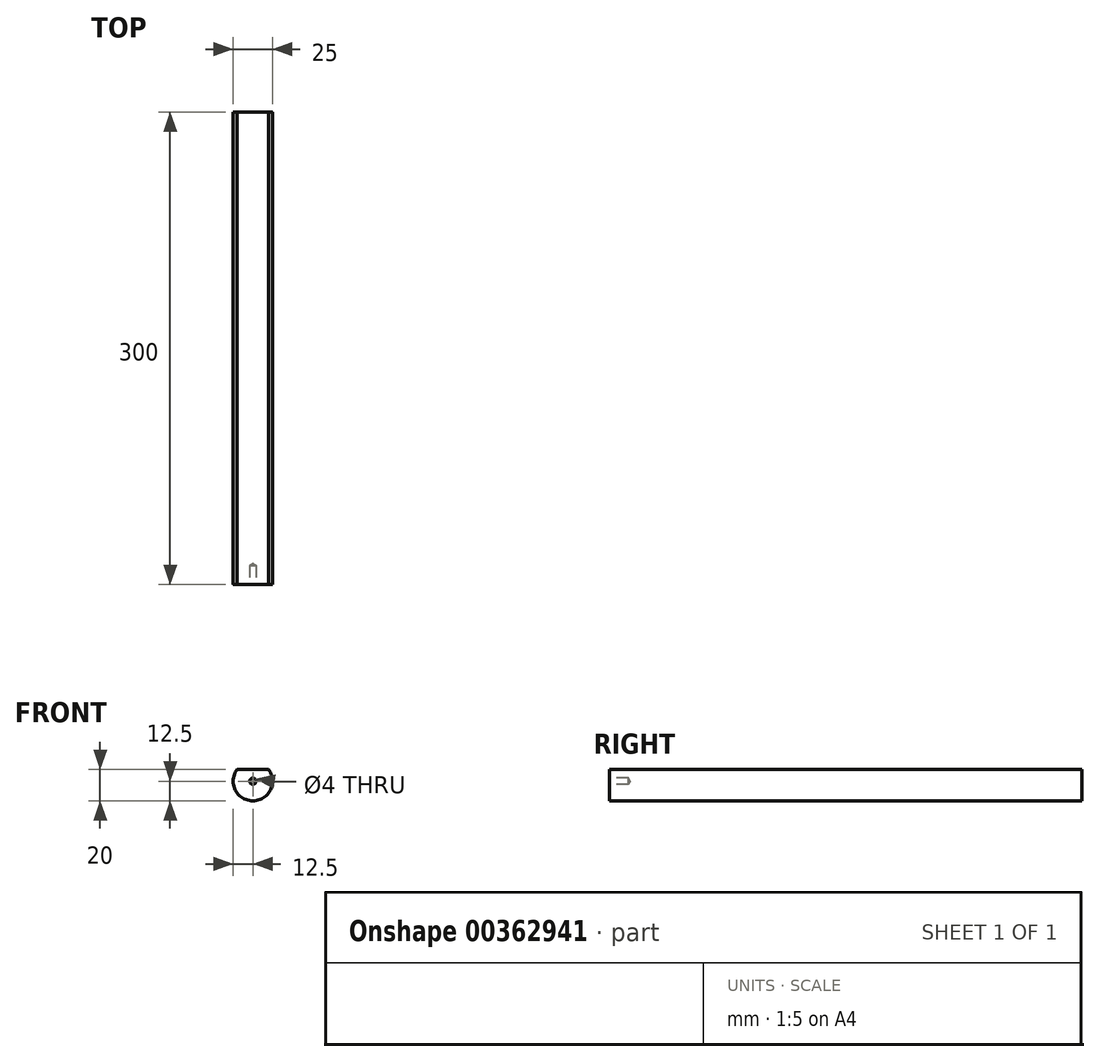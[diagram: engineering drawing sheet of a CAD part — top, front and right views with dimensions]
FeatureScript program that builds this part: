
annotation { "Feature Type Name" : "Feature", "Feature Type Description" : "" }
export const myFeature = defineFeature(function(context is Context, id is Id, definition is map)
    precondition{}
    {
        {
            var Q0;
            Q0=qCreatedBy(makeId("Front.planeOp"),FACE);
            var sketch = newSketch(context, id + "F0", { "sketchPlane" : qUnion([Q0])});
            skArc(sketch, "E0", {"start": v(-10, 7.5) * mm, "mid": v(0, -12.5) * mm, "end": v(10, 7.5) * mm});
            skLineSegment(sketch, "E1", {"start": v(-10, 7.5) * mm, "end": v(10, 7.5) * mm});
            skSolve(sketch);
        }
        {
            var Q0;
            Q0=makeQuery(id+"F0.imprint","IMPRINT",FACE,{"disambiguationData":[TD([[makeQuery(id+"F0.imprint","IMPRINT",EDGE,{"derivedFrom":sQuery(id+"F0.wireOp",EDGE,"E0")}),1.0]])]});
            extrude(context, id + "F1", {"entities" : qUnion([Q0]), "depth" : 300 * mm});
        }
        {
            var Q0;
            Q0=makeQuery(id+"F1.opExtrude","CAP_FACE",FACE,{"disambiguationData":[OSD([sQuery(id+"F0.wireOp",EDGE,"E0"),sQuery(id+"F0.wireOp",EDGE,"E1")])],"isStart":false});
            var sketch = newSketch(context, id + "F2", { "sketchPlane" : qUnion([Q0])});
            skCircle(sketch, "E2", {"center": v(0, 0) * mm, "radius": 2 * mm});
            skSolve(sketch);
        }
        {
            var Q0;
            Q0=sQuery(id+"F2.wireOp",VERTEX,"E2.center");
            var Q1;
            Q1=makeQuery(id+"F1.opExtrude","SWEPT_BODY",BODY,{"disambiguationData":[OSD([sQuery(id+"F0.wireOp",EDGE,"E0"),sQuery(id+"F0.wireOp",EDGE,"E1")])]});
            hole(context, id + "F3", {"style" : HoleStyle.SIMPLE, "endStyle" : HoleEndStyle.BLIND, "holeDiameter" : 4 * mm, "holeDepth" : 12 * mm, "isTappedThrough" : true, "tappedDepth" : 12 * mm, "tapClearance" : 3, "locations" : qUnion([Q0]), "scope" : qUnion([Q1])});
        }
    });
